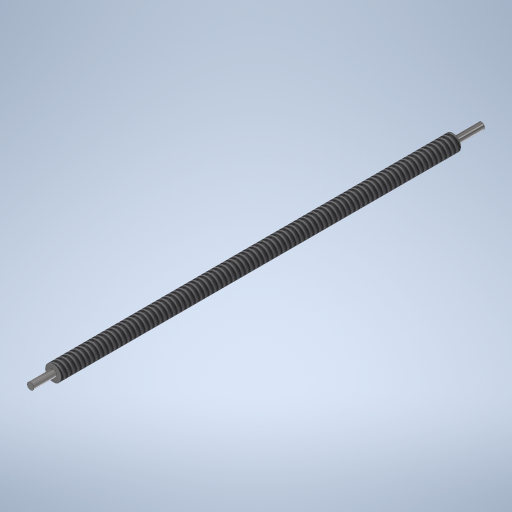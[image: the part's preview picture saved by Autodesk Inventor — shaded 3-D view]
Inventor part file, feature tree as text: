
AUTODESK INVENTOR PART (.ipt)
format: ipt  version: 2023 (Build 270158000, 158)  size: 315,904 bytes
history: native  units: mm
features: other x2, sketch x2, helix x1, thread x1
ambient origin geometry x8: Origin, YZ Plane, XZ Plane, XY Plane, X Axis, Y Axis, Z Axis, Center Point
bodies: Body1 (feature_tree)
feature tree (6):
  other  "Sólido1"
  other  "Revolução1"
  helix  "Coil1"  [1 undecoded]
  thread  "Thread2"  [1 undecoded]
  sketch  "Esboço1"  dims[d2=4.0mm]
  sketch  "Sketch3"  dims[d3=350.0mm d4=4.0mm d5=25.0mm d6=90.0deg d10=2.0mm d11=1.0mm d12=1.0mm d13=0.0mm d14=4.0mm d15=200.0mm d16=1000.0mm d17=0.0mm d18=90.0deg d19=90.0deg d20=0.0mm d21=0.0mm d22=350.0mm d23=0.0mm]
note: 2 required parameter values undecoded (feature->parameter linkage not recoverable at this tier; creation-order binding heuristic only, values carry confidence <= 0.55)
